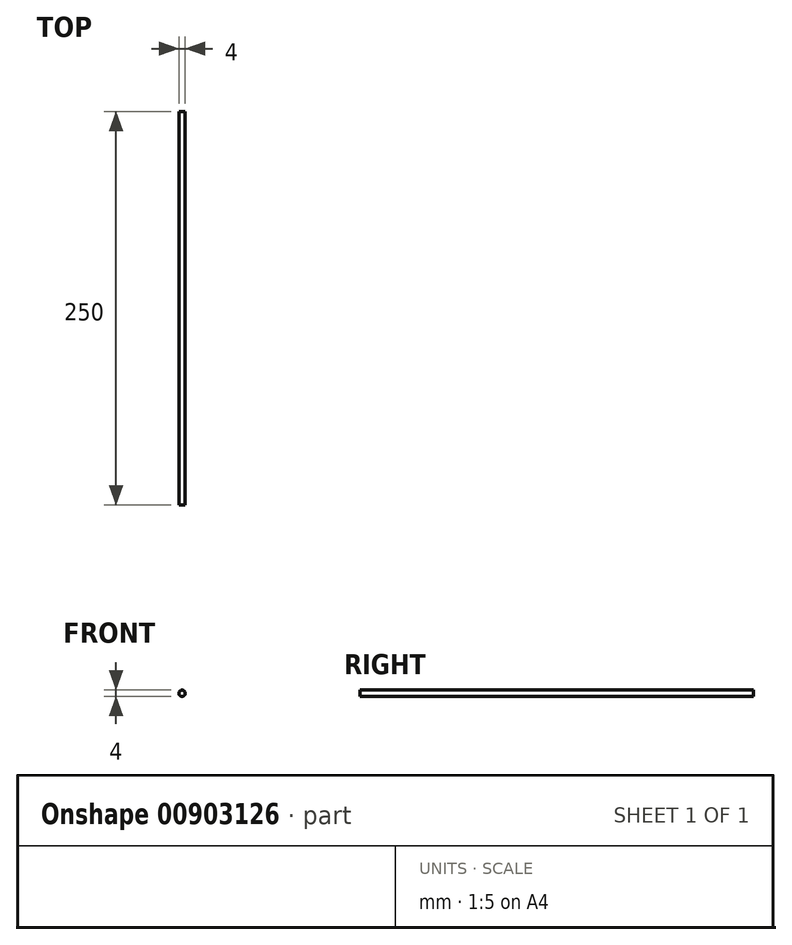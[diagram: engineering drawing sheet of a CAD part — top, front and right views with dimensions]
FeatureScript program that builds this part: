
annotation { "Feature Type Name" : "Feature", "Feature Type Description" : "" }
export const myFeature = defineFeature(function(context is Context, id is Id, definition is map)
    precondition{}
    {
        {
            var Q0;
            Q0=qCreatedBy(makeId("Front.planeOp"),FACE);
            var sketch = newSketch(context, id + "F0", { "sketchPlane" : qUnion([Q0])});
            skCircle(sketch, "E0", {"center": v(0, 0) * mm, "radius": 2 * mm});
            skSolve(sketch);
        }
        {
            var Q0;
            Q0=qSketchRegion(id+"F0",true);
            extrude(context, id + "F1", {"entities" : qUnion([Q0]), "depth" : 250 * mm, "offsetDistance" : 25 * mm});
        }
    });
